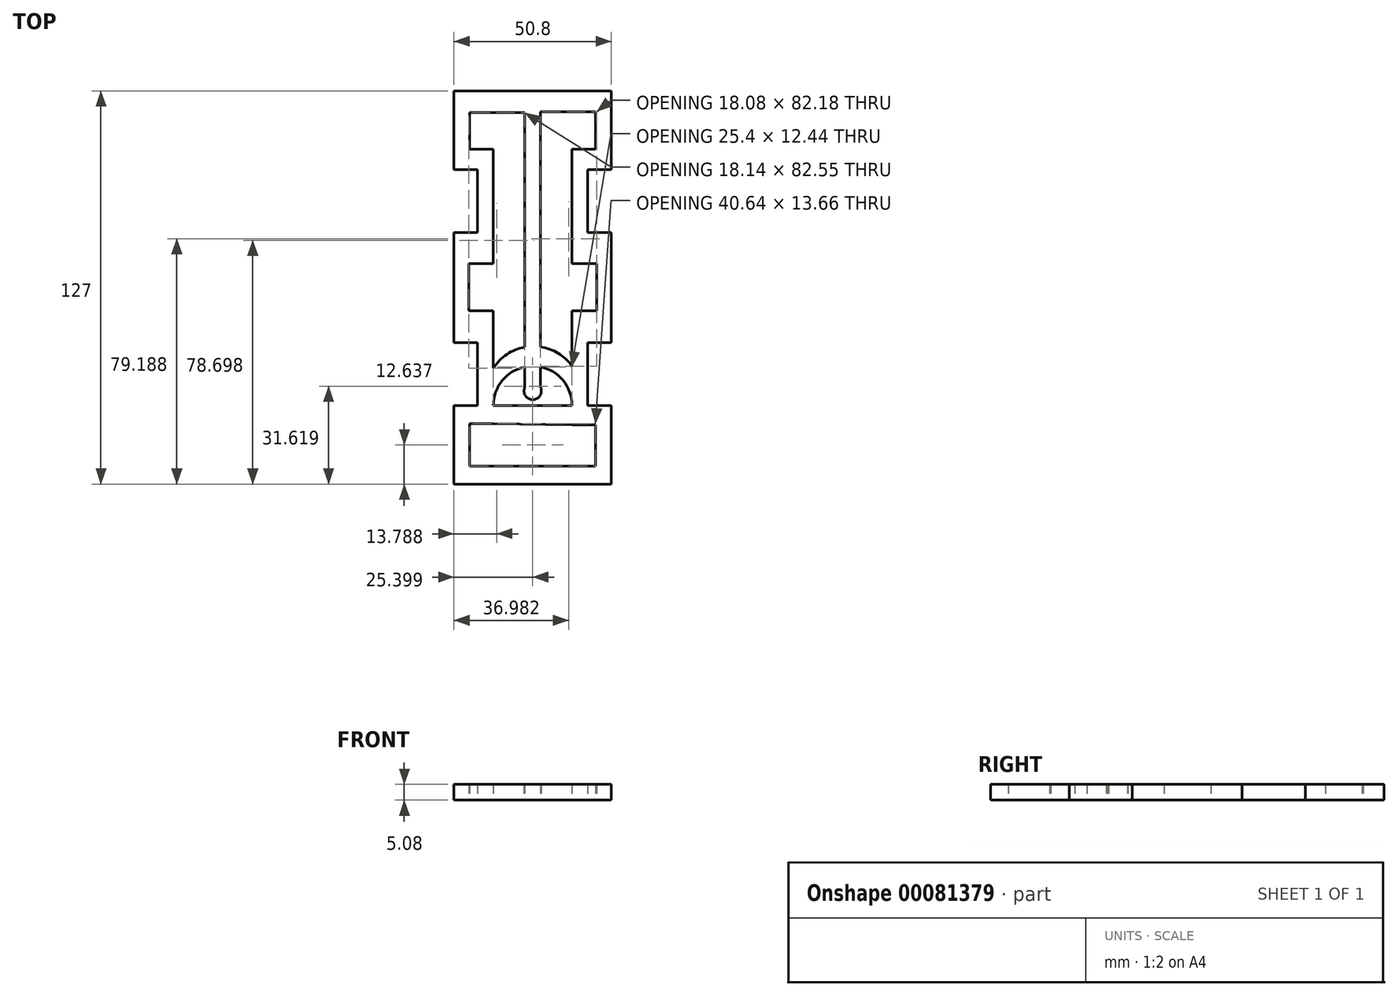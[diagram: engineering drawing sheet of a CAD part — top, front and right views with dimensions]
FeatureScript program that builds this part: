
annotation { "Feature Type Name" : "Feature", "Feature Type Description" : "" }
export const myFeature = defineFeature(function(context is Context, id is Id, definition is map)
    precondition{}
    {
        {
            var Q0;
            Q0=qCreatedBy(makeId("Top.planeOp"),FACE);
            var sketch = newSketch(context, id + "F0", { "sketchPlane" : qUnion([Q0])});
            skLineSegment(sketch, "E0.bottom", {"start": v(-55.07, 55.76) * mm, "end": v(-4.27, 55.76) * mm});
            skLineSegment(sketch, "E0.top", {"start": v(-55.07, -71.24) * mm, "end": v(-4.27, -71.24) * mm});
            skLineSegment(sketch, "E0.left", {"start": v(-55.07, 55.76) * mm, "end": v(-55.07, 30.36) * mm});
            skLineSegment(sketch, "E0.right", {"start": v(-4.27, 55.76) * mm, "end": v(-4.27, 30.36) * mm});
            skLineSegment(sketch, "E1.bottom", {"start": v(-55.07, 30.36) * mm, "end": v(-47.45, 30.36) * mm});
            skLineSegment(sketch, "E1.top", {"start": v(-55.07, 10.04) * mm, "end": v(-47.45, 10.04) * mm});
            skLineSegment(sketch, "E1.right", {"start": v(-47.45, 30.36) * mm, "end": v(-47.45, 10.04) * mm});
            skLineSegment(sketch, "E2.bottom", {"start": v(-55.07, -25.52) * mm, "end": v(-47.45, -25.52) * mm});
            skLineSegment(sketch, "E2.top", {"start": v(-55.07, -45.84) * mm, "end": v(-47.45, -45.84) * mm});
            skLineSegment(sketch, "E2.right", {"start": v(-47.45, -25.52) * mm, "end": v(-47.45, -45.84) * mm});
            skLineSegment(sketch, "E3.bottom", {"start": v(-4.27, 30.36) * mm, "end": v(-11.9, 30.36) * mm});
            skLineSegment(sketch, "E3.top", {"start": v(-4.27, 10.04) * mm, "end": v(-11.9, 10.04) * mm});
            skLineSegment(sketch, "E3.right", {"start": v(-11.9, 30.36) * mm, "end": v(-11.9, 10.04) * mm});
            skLineSegment(sketch, "E4.bottom", {"start": v(-4.27, -25.52) * mm, "end": v(-11.9, -25.52) * mm});
            skLineSegment(sketch, "E4.top", {"start": v(-4.27, -45.84) * mm, "end": v(-11.9, -45.84) * mm});
            skLineSegment(sketch, "E4.right", {"start": v(-11.9, -25.52) * mm, "end": v(-11.9, -45.84) * mm});
            skLineSegment(sketch, "E5.trimOffspring", {"start": v(-55.07, 10.04) * mm, "end": v(-55.07, -25.52) * mm});
            skLineSegment(sketch, "E6.trimOffspring", {"start": v(-55.07, -45.84) * mm, "end": v(-55.07, -71.24) * mm});
            skLineSegment(sketch, "E7.trimOffspring", {"start": v(-4.27, -45.84) * mm, "end": v(-4.27, -71.24) * mm});
            skLineSegment(sketch, "E8.trimOffspring", {"start": v(-4.27, 10.04) * mm, "end": v(-4.27, -25.52) * mm});
            skLineSegment(sketch, "E9.bottom", {"start": v(-42.37, 48.73) * mm, "end": v(-32.21, 48.73) * mm});
            skLineSegment(sketch, "E9.left", {"start": v(-42.37, 36.9) * mm, "end": v(-42.37, 0) * mm});
            skLineSegment(sketch, "E9.right", {"start": v(-32.21, 48.73) * mm, "end": v(-32.21, -27) * mm});
            skLineSegment(sketch, "E10.bottom", {"start": v(-27.13, 49.04) * mm, "end": v(-16.97, 49.04) * mm});
            skLineSegment(sketch, "E11.bottom", {"start": v(-50, 48.73) * mm, "end": v(-42.37, 48.73) * mm});
            skLineSegment(sketch, "E11.top", {"start": v(-50, 36.9) * mm, "end": v(-42.37, 36.9) * mm});
            skLineSegment(sketch, "E11.left", {"start": v(-50, 48.73) * mm, "end": v(-50, 36.9) * mm});
            skLineSegment(sketch, "E12.bottom", {"start": v(-16.97, 49.04) * mm, "end": v(-9.35, 49.04) * mm});
            skLineSegment(sketch, "E12.top", {"start": v(-16.97, 36.9) * mm, "end": v(-9.35, 36.9) * mm});
            skLineSegment(sketch, "E12.right", {"start": v(-9.35, 49.04) * mm, "end": v(-9.35, 36.9) * mm});
            skLineSegment(sketch, "E13.bottom", {"start": v(-42.37, -51.77) * mm, "end": v(-50, -51.77) * mm});
            skLineSegment(sketch, "E13.right", {"start": v(-50, -51.77) * mm, "end": v(-50, -65.44) * mm});
            skLineSegment(sketch, "E14.bottom", {"start": v(-16.97, -52.07) * mm, "end": v(-9.35, -52.07) * mm});
            skLineSegment(sketch, "E14.right", {"start": v(-9.35, -52.07) * mm, "end": v(-9.35, -65.44) * mm});
            skLineSegment(sketch, "E15", {"start": v(-16.97, -33.14) * mm, "end": v(-16.97, -15.24) * mm});
            skLineSegment(sketch, "E16.bottom", {"start": v(-42.37, 0) * mm, "end": v(-50.35, 0) * mm});
            skLineSegment(sketch, "E16.top", {"start": v(-42.37, -15.24) * mm, "end": v(-50.35, -15.24) * mm});
            skLineSegment(sketch, "E16.right", {"start": v(-50.35, 0) * mm, "end": v(-50.35, -15.24) * mm});
            skLineSegment(sketch, "E17.bottom", {"start": v(-16.97, 0) * mm, "end": v(-9.05, 0) * mm});
            skLineSegment(sketch, "E17.top", {"start": v(-16.97, -15.24) * mm, "end": v(-9.05, -15.24) * mm});
            skLineSegment(sketch, "E17.right", {"start": v(-9.05, 0) * mm, "end": v(-9.05, -15.24) * mm});
            skLineSegment(sketch, "E18.trimOffspring", {"start": v(-42.37, -15.24) * mm, "end": v(-42.37, -33.82) * mm});
            skLineSegment(sketch, "E19.trimOffspring", {"start": v(-16.97, 0) * mm, "end": v(-16.97, 36.9) * mm});
            skLineSegment(sketch, "E20", {"start": v(-50, -65.44) * mm, "end": v(-9.35, -65.44) * mm});
            skLineSegment(sketch, "E21", {"start": v(-27.13, -52.47) * mm, "end": v(-27.13, -65.44) * mm});
            skLineSegment(sketch, "E22", {"start": v(-32.21, -52.47) * mm, "end": v(-32.21, -65.44) * mm});
            skLineSegment(sketch, "E23", {"start": v(-42.37, -51.77) * mm, "end": v(-16.97, -52.07) * mm});
            skLineSegment(sketch, "E24", {"start": v(-42.37, -45.84) * mm, "end": v(-16.97, -45.84) * mm});
            skLineSegment(sketch, "E25.trimOffspring", {"start": v(-27.13, -51.95) * mm, "end": v(-27.13, -52.47) * mm});
            skLineSegment(sketch, "E26.trimOffspring", {"start": v(-32.21, -51.9) * mm, "end": v(-32.21, -52.47) * mm});
            skArc(sketch, "E27", {"start": v(-16.97, -45.84) * mm, "mid": v(-19.83, -37.81) * mm, "end": v(-27.13, -33.4) * mm});
            skArc(sketch, "E28", {"start": v(-16.97, -33.14) * mm, "mid": v(-21.42, -29) * mm, "end": v(-27.13, -26.92) * mm});
            skPoint(sketch, "E28.startSnap0", {"position": v(-29.67, -33.14) * mm});
            skLineSegment(sketch, "E29", {"start": v(-32.21, -33.4) * mm, "end": v(-32.21, -40.01) * mm});
            skLineSegment(sketch, "E30", {"start": v(-27.13, -33.4) * mm, "end": v(-27.13, -40.01) * mm});
            skArc(sketch, "E31", {"start": v(-32.21, -40.01) * mm, "mid": v(-29.67, -44) * mm, "end": v(-27.13, -40.01) * mm});
            skArc(sketch, "E32.trimOffspring", {"start": v(-32.21, -27) * mm, "mid": v(-38, -29.35) * mm, "end": v(-42.37, -33.82) * mm});
            skArc(sketch, "E33.trimOffspring", {"start": v(-32.21, -33.4) * mm, "mid": v(-39.5, -37.81) * mm, "end": v(-42.37, -45.84) * mm});
            skLineSegment(sketch, "E34", {"start": v(-27.13, -26.92) * mm, "end": v(-27.13, 49.04) * mm});
            skSolve(sketch);
        }
        {
            var Q0;
            Q0=makeQuery(id+"F0.imprint","IMPRINT",FACE,{"disambiguationData":[TD([[makeQuery(id+"F0.imprint","IMPRINT",EDGE,{"derivedFrom":sQuery(id+"F0.wireOp",EDGE,"E0.bottom")}),-1.0]])]});
            extrude(context, id + "F1", {"entities" : qUnion([Q0]), "depth" : 5.08 * mm});
        }
    });
